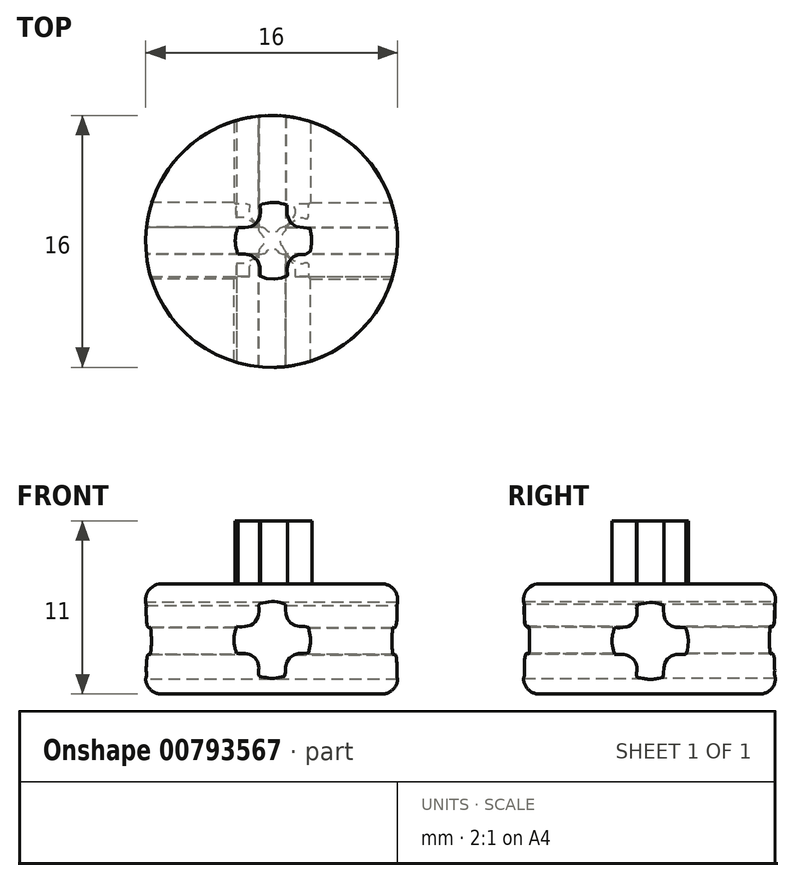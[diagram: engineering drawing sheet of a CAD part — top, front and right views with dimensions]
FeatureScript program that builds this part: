
annotation { "Feature Type Name" : "Feature", "Feature Type Description" : "" }
export const myFeature = defineFeature(function(context is Context, id is Id, definition is map)
    precondition{}
    {
        {
            var Q0;
            Q0=qCreatedBy(makeId("Top.planeOp"),FACE);
            var sketch = newSketch(context, id + "F0", { "sketchPlane" : qUnion([Q0])});
            skCircle(sketch, "E0", {"center": v(0, 0) * mm, "radius": 8 * mm});
            skSolve(sketch);
        }
        {
            var Q0;
            Q0=makeQuery(id+"F0.imprint","IMPRINT",FACE,{"disambiguationData":[TD([[makeQuery(id+"F0.imprint","IMPRINT",EDGE,{"derivedFrom":sQuery(id+"F0.wireOp",EDGE,"E0")}),1.0]])]});
            extrude(context, id + "F1", {"entities" : qUnion([Q0]), "depth" : 7 * mm, "offsetDistance" : 25 * mm});
        }
        {
            var Q0;
            Q0=makeQuery(id+"F1.opExtrude","CAP_FACE",FACE,{"disambiguationData":[OSD([sQuery(id+"F0.wireOp",EDGE,"E0")])],"isStart":false});
            var sketch = newSketch(context, id + "F2", { "sketchPlane" : qUnion([Q0])});
            skFitSpline(sketch, "E1", {"points": [v(-2.15, -0.81) * mm, v(-2.31, 0.07) * mm, v(-2.15, 0.89) * mm], "startDerivative": vector(-0.5, 1.75) * mm, "endDerivative": vector(0.5, 1.65) * mm});
            skFitSpline(sketch, "E2", {"points": [v(-2.15, 0.89) * mm, v(-1.58, 0.89) * mm, v(-1.15, 1.04) * mm, v(-0.85, 1.35) * mm, v(-0.73, 1.7) * mm, v(-0.72, 2.1) * mm, v(-0.72, 2.3) * mm, v(-0.48, 2.39) * mm, v(-0.1, 2.46) * mm, v(0.24, 2.47) * mm, v(0.56, 2.43) * mm, v(0.98, 2.3) * mm], "startDerivative": vector(5.18, -0.26) * mm, "endDerivative": vector(4.37, -1.41) * mm});
            skFitSpline(sketch, "E3", {"points": [v(-2.15, -0.81) * mm, v(-1.85, -0.81) * mm, v(-1.6, -0.81) * mm, v(-1.41, -0.84) * mm, v(-1.07, -1.01) * mm, v(-0.89, -1.21) * mm, v(-0.76, -1.47) * mm, v(-0.72, -1.8) * mm, v(-0.72, -2.23) * mm, v(-0.44, -2.32) * mm, v(-0.16, -2.38) * mm, v(0.17, -2.4) * mm, v(0.46, -2.37) * mm, v(0.72, -2.31) * mm, v(0.98, -2.23) * mm, v(0.98, -2.04) * mm, v(0.98, -1.72) * mm, v(1.01, -1.48) * mm, v(1.1, -1.29) * mm, v(1.27, -1.06) * mm, v(1.4, -0.96) * mm, v(1.58, -0.87) * mm, v(1.83, -0.81) * mm, v(2.08, -0.81) * mm, v(2.4, -0.81) * mm, v(2.48, -0.56) * mm, v(2.54, -0.2) * mm, v(2.55, 0.07) * mm, v(2.53, 0.34) * mm, v(2.46, 0.7) * mm, v(2.4, 0.89) * mm, v(2.08, 0.89) * mm, v(1.8, 0.9) * mm, v(1.47, 1) * mm, v(1.28, 1.13) * mm, v(1.07, 1.4) * mm, v(0.98, 1.81) * mm, v(0.98, 2.3) * mm], "startDerivative": vector(10.87, -0.02) * mm, "endDerivative": vector(0.52, 14.17) * mm});
            skSolve(sketch);
        }
        {
            var Q0;
            Q0=makeQuery(id+"F2.imprint","IMPRINT",FACE,{"disambiguationData":[TD([[makeQuery(id+"F2.imprint","IMPRINT",EDGE,{"derivedFrom":sQuery(id+"F2.wireOp",EDGE,"E1")}),-1.0]])]});
            extrude(context, id + "F3", {"entities" : qUnion([Q0]), "operationType" : NewBodyOperationType.ADD, "depth" : 4 * mm, "offsetDistance" : 25 * mm});
        }
        {
            var Q0;
            Q0=qCreatedBy(makeId("Right.planeOp"),FACE);
            var sketch = newSketch(context, id + "F4", { "sketchPlane" : qUnion([Q0])});
            skFitSpline(sketch, "E4", {"points": [v(-2.22, 2.52) * mm, v(-2.39, 3.4) * mm, v(-2.22, 4.22) * mm], "startDerivative": vector(-0.5, 1.75) * mm, "endDerivative": vector(0.5, 1.65) * mm});
            skFitSpline(sketch, "E5", {"points": [v(-2.22, 4.22) * mm, v(-1.66, 4.22) * mm, v(-1.22, 4.37) * mm, v(-0.92, 4.68) * mm, v(-0.8, 5.03) * mm, v(-0.8, 5.44) * mm, v(-0.8, 5.64) * mm, v(-0.56, 5.72) * mm, v(-0.17, 5.8) * mm, v(0.17, 5.8) * mm, v(0.49, 5.76) * mm, v(0.9, 5.64) * mm], "startDerivative": vector(5.18, -0.26) * mm, "endDerivative": vector(4.37, -1.41) * mm});
            skFitSpline(sketch, "E6", {"points": [v(-2.22, 2.52) * mm, v(-1.93, 2.52) * mm, v(-1.68, 2.52) * mm, v(-1.49, 2.5) * mm, v(-1.15, 2.32) * mm, v(-0.96, 2.12) * mm, v(-0.84, 1.86) * mm, v(-0.8, 1.54) * mm, v(-0.8, 1.1) * mm, v(-0.52, 1.01) * mm, v(-0.23, 0.95) * mm, v(0.1, 0.93) * mm, v(0.38, 0.96) * mm, v(0.65, 1.02) * mm, v(0.9, 1.1) * mm, v(0.9, 1.3) * mm, v(0.9, 1.6) * mm, v(0.94, 1.86) * mm, v(1.02, 2.05) * mm, v(1.2, 2.27) * mm, v(1.33, 2.38) * mm, v(1.5, 2.47) * mm, v(1.76, 2.52) * mm, v(2, 2.52) * mm, v(2.32, 2.52) * mm, v(2.4, 2.78) * mm, v(2.46, 3.13) * mm, v(2.47, 3.4) * mm, v(2.46, 3.67) * mm, v(2.38, 4.04) * mm, v(2.32, 4.22) * mm, v(2, 4.22) * mm, v(1.73, 4.23) * mm, v(1.4, 4.33) * mm, v(1.2, 4.46) * mm, v(1, 4.73) * mm, v(0.9, 5.15) * mm, v(0.9, 5.64) * mm], "startDerivative": vector(10.87, -0.02) * mm, "endDerivative": vector(0.52, 14.17) * mm});
            skSolve(sketch);
        }
        {
            var Q0;
            Q0 = qSketchRegion(id + "F4", true);
            extrude(context, id + "F5", {"entities" : qUnion([Q0]), "operationType" : NewBodyOperationType.REMOVE, "oppositeDirection" : true, "depth" : 25 * mm, "offsetDistance" : 25 * mm, "hasSecondDirection" : true, "secondDirectionOppositeDirection" : false, "secondDirectionDepth" : 25 * mm});
        }
        {
            var Q0;
            Q0=qCreatedBy(makeId("Front.planeOp"),FACE);
            var sketch = newSketch(context, id + "F6", { "sketchPlane" : qUnion([Q0])});
            skFitSpline(sketch, "E7", {"points": [v(-2.23, 2.59) * mm, v(-2.4, 3.47) * mm, v(-2.23, 4.29) * mm], "startDerivative": vector(-0.5, 1.75) * mm, "endDerivative": vector(0.5, 1.65) * mm});
            skFitSpline(sketch, "E8", {"points": [v(-2.23, 4.29) * mm, v(-1.67, 4.29) * mm, v(-1.23, 4.43) * mm, v(-0.93, 4.75) * mm, v(-0.82, 5.1) * mm, v(-0.81, 5.5) * mm, v(-0.81, 5.7) * mm, v(-0.57, 5.79) * mm, v(-0.18, 5.86) * mm, v(0.16, 5.87) * mm, v(0.48, 5.83) * mm, v(0.9, 5.7) * mm], "startDerivative": vector(5.18, -0.26) * mm, "endDerivative": vector(4.37, -1.41) * mm});
            skFitSpline(sketch, "E9", {"points": [v(-2.23, 2.59) * mm, v(-1.94, 2.59) * mm, v(-1.69, 2.58) * mm, v(-1.5, 2.55) * mm, v(-1.16, 2.38) * mm, v(-0.97, 2.19) * mm, v(-0.85, 1.92) * mm, v(-0.81, 1.6) * mm, v(-0.81, 1.16) * mm, v(-0.53, 1.08) * mm, v(-0.24, 1.02) * mm, v(0.09, 1) * mm, v(0.37, 1.02) * mm, v(0.64, 1.08) * mm, v(0.9, 1.16) * mm, v(0.9, 1.36) * mm, v(0.9, 1.67) * mm, v(0.93, 1.92) * mm, v(1, 2.11) * mm, v(1.18, 2.33) * mm, v(1.32, 2.44) * mm, v(1.5, 2.53) * mm, v(1.75, 2.58) * mm, v(2, 2.59) * mm, v(2.31, 2.59) * mm, v(2.4, 2.84) * mm, v(2.45, 3.2) * mm, v(2.46, 3.47) * mm, v(2.45, 3.73) * mm, v(2.37, 4.1) * mm, v(2.31, 4.29) * mm, v(2, 4.29) * mm, v(1.72, 4.3) * mm, v(1.39, 4.4) * mm, v(1.2, 4.53) * mm, v(0.99, 4.8) * mm, v(0.9, 5.2) * mm, v(0.9, 5.7) * mm], "startDerivative": vector(10.87, -0.02) * mm, "endDerivative": vector(0.52, 14.17) * mm});
            skSolve(sketch);
        }
        {
            var Q0;
            Q0 = qSketchRegion(id + "F6", true);
            extrude(context, id + "F7", {"entities" : qUnion([Q0]), "operationType" : NewBodyOperationType.REMOVE, "oppositeDirection" : true, "depth" : 25 * mm, "offsetDistance" : 25 * mm, "hasSecondDirection" : true, "secondDirectionOppositeDirection" : false, "secondDirectionDepth" : 25 * mm});
        }
        {
            var Q0;
            Q0=makeQuery(id+"F1.opExtrude","CAP_EDGE",EDGE,{"disambiguationData":[OSD([sQuery(id+"F0.wireOp",EDGE,"E0")])],"isStart":true});
            var Q1;
            Q1=makeQuery(id+"F1.opExtrude","CAP_EDGE",EDGE,{"disambiguationData":[OSD([sQuery(id+"F0.wireOp",EDGE,"E0")])],"isStart":false});
            fillet(context, id + "F8", {"entities" : qUnion([Q0, Q1]), "radius" : 1 * mm, "tangentPropagation" : true, "allowEdgeOverflow" : false});
        }
    });
